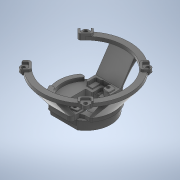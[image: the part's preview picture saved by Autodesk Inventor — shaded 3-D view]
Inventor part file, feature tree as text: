
AUTODESK INVENTOR PART (.ipt)
format: ipt  version: 2020 (Build 240168000, 168)  size: 1,461,248 bytes
history: native  units: mm
features: projected_geometry x52, sketch x31, extrude x24, other x9, fillet x9, chamfer x4, loft x2, revolve x1, pattern_circular x1, mirror x1
ambient origin geometry x8: Origin, YZ Plane, XZ Plane, XY Plane, X Axis, Y Axis, Z Axis, Center Point
bodies: Body1 (feature_tree)
feature tree (134):
  other  "Твердое тело1"
  extrude  "Выдавливание1"  Depth=17.1mm
  extrude  "Выдавливание2"  Depth=17.1mm
  other  "РабПлоскость1"
  sketch  "Эскиз3"
  other  "РабОсь1"
  revolve  "Вращение1"
  extrude  "Выдавливание3"  Depth=25.0mm
  extrude  "Выдавливание4"  Depth=5.3mm
  extrude  "Выдавливание5"  Depth=44.7mm
  extrude  "Выдавливание6"  Depth=7.7mm TaperAngle=0.0deg
  extrude  "Выдавливание7"  Depth=5.0mm
  extrude  "Выдавливание8"  Depth=30.65mm
  sketch  "Эскиз10"
  extrude  "Выдавливание9"  Depth=2.5mm TaperAngle=0.0deg
  fillet  "Сопряжение1"  Radius=0.2mm
  fillet  "Сопряжение2"  [1 undecoded]
  fillet  "Сопряжение3"  Radius=1.85mm
  extrude  "Выдавливание10"  Depth=30.0mm
  fillet  "Сопряжение4"  Radius=2.0mm
  fillet  "Сопряжение5"  Radius=3.0mm
  extrude  "камера"  Depth=38.0mm
  extrude  "труба"  Depth=10.0mm TaperAngle=0.0deg
  sketch  "Эскиз15"
  other  "РабПлоскость2"
  extrude  "Выдавливание12"  Depth=5.2mm
  extrude  "Выдавливание13"  Depth=6.2mm
  chamfer  "Фаска1"  Distance=29.46mm
  fillet  "Сопряжение6"  Radius=10.0mm
  fillet  "Сопряжение7"  Radius=9.5mm
  other  "РабОсь2"
  pattern_circular  "Круговой массив1"  [2 undecoded]
  extrude  "Выдавливание15"  TaperAngle=60.0deg  [1 undecoded]
  chamfer  "Фаска2"  Distance=6.0mm
  sketch  "Эскиз20"
  extrude  "Выдавливание16"  Depth=6.0mm
  fillet  "Сопряжение8"  Radius=14.2mm
  other  "РабПлоскость3"
  extrude  "Выдавливание17"  Depth=9.5mm
  extrude  "Выдавливание18"  Depth=2.0mm
  sketch  "Эскиз24"
  sketch  "Эскиз25"
  sketch  "Эскиз26"
  extrude  "Выдавливание19"  Depth=13.962634mm
  loft  "Лофт1"
  other  "РабПлоскость4"
  mirror  "Зеркальное отражение1"
  extrude  "Выдавливание20"  Depth=2.0mm TaperAngle=0.0deg
  loft  "Лофт2"
  extrude  "Выдавливание21"  Depth=6.2mm
  chamfer  "Фаска3"  Distance=6.0mm
  chamfer  "Фаска4"  Distance=1.7mm
  extrude  "Выдавливание22"  Depth=1.5mm TaperAngle=0.0deg
  extrude  "Выдавливание23"  Depth=6.0mm TaperAngle=0.0deg
  fillet  "Сопряжение9"  Radius=0.5mm
  extrude  "Выдавливание24"  Depth=0.7mm
  sketch  "Эскиз1"
  sketch  "Эскиз2"
  projected_geometry  "Спроецированная петля1"
  projected_geometry  "Спроецированная петля2"
  sketch  "Эскиз4"
  projected_geometry  "Спроецированная петля3"
  sketch  "Эскиз5"
  sketch  "Эскиз6"
  projected_geometry  "Спроецированная петля4"
  sketch  "Эскиз7"
  projected_geometry  "Спроецированная петля5"
  sketch  "Эскиз8"
  projected_geometry  "Спроецированная петля6"
  projected_geometry  "Спроецированная петля7"
  projected_geometry  "Спроецированная петля8"
  sketch  "Эскиз9"
  projected_geometry  "Спроецированная петля9"
  projected_geometry  "Спроецированная петля10"
  projected_geometry  "Спроецированная петля11"
  projected_geometry  "Спроецированная петля12"
  sketch  "Эскиз11"
  sketch  "Эскиз12"
  projected_geometry  "Спроецированная петля13"
  projected_geometry  "Спроецированная петля14"
  projected_geometry  "Спроецированная петля15"
  sketch  "Эскиз14"
  projected_geometry  "Спроецированная петля20"
  projected_geometry  "Спроецированная петля21"
  projected_geometry  "Спроецированная петля22"
  projected_geometry  "Спроецированная петля23"
  sketch  "Эскиз16"
  projected_geometry  "Спроецированная петля24"
  sketch  "Эскиз17"
  projected_geometry  "Спроецированная петля25"
  sketch  "Эскиз18"
  sketch  "Эскиз19"
  projected_geometry  "Спроецированная петля26"
  projected_geometry  "Спроецированная петля27"
  projected_geometry  "Спроецированная петля28"
  projected_geometry  "Спроецированная петля29"
  sketch  "Эскиз21"
  projected_geometry  "Спроецированная петля30"
  projected_geometry  "Спроецированная петля31"
  projected_geometry  "Спроецированная петля32"
  projected_geometry  "Спроецированная петля33"
  projected_geometry  "Спроецированная петля34"
  projected_geometry  "Спроецированная петля35"
  projected_geometry  "Спроецированная петля36"
  projected_geometry  "Спроецированная петля37"
  projected_geometry  "Спроецированная петля38"
  projected_geometry  "Спроецированная петля39"
  sketch  "Эскиз22"
  projected_geometry  "Спроецированная петля40"
  projected_geometry  "Спроецированная петля41"
  projected_geometry  "Спроецированная петля42"
  projected_geometry  "Спроецированная петля43"
  projected_geometry  "Спроецированная петля44"
  sketch  "Эскиз23"
  projected_geometry  "Спроецированная петля45"
  projected_geometry  "Спроецированная петля46"
  projected_geometry  "Спроецированная петля47"
  projected_geometry  "Спроецированная петля48"
  projected_geometry  "Спроецированная петля49"
  projected_geometry  "Спроецированная петля50"
  other  "Ребра1"
  sketch  "Эскиз27"
  projected_geometry  "Спроецированная петля51"
  sketch  "Эскиз28"
  projected_geometry  "Спроецированная петля52"
  projected_geometry  "Спроецированная петля53"
  other  "Ребра2"
  sketch  "Эскиз31"
  sketch  "Эскиз32"
  projected_geometry  "Спроецированная петля54"
  projected_geometry  "Спроецированная петля55"
  sketch  "Эскиз33"
  projected_geometry  "Спроецированная петля56"
  sketch  "Эскиз34"
note: 4 required parameter values undecoded (feature->parameter linkage not recoverable at this tier; creation-order binding heuristic only, values carry confidence <= 0.55)
